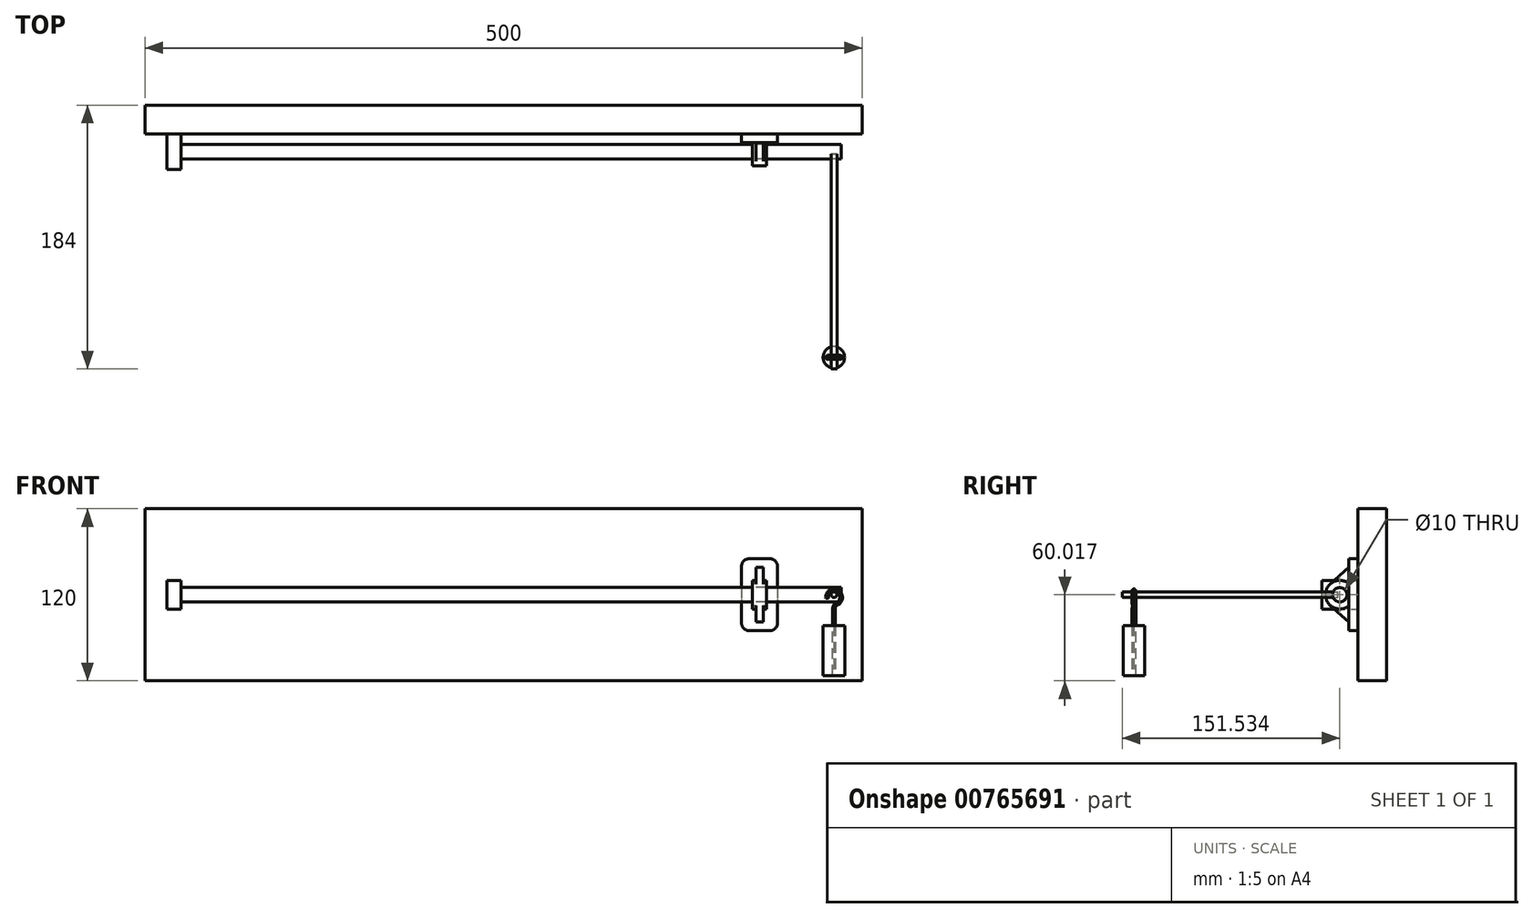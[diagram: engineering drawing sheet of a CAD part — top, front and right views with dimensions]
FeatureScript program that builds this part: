
annotation { "Feature Type Name" : "Feature", "Feature Type Description" : "" }
export const myFeature = defineFeature(function(context is Context, id is Id, definition is map)
    precondition{}
    {
        {
            var Q0;
            Q0=qCreatedBy(makeId("Front.planeOp"),FACE);
            var sketch = newSketch(context, id + "F0", { "sketchPlane" : qUnion([Q0])});
            skLineSegment(sketch, "E0.bottom", {"start": v(-32.37, 28.17) * mm, "end": v(467.63, 28.17) * mm});
            skLineSegment(sketch, "E0.top", {"start": v(-32.37, -91.83) * mm, "end": v(467.63, -91.83) * mm});
            skLineSegment(sketch, "E0.left", {"start": v(-32.37, 28.17) * mm, "end": v(-32.37, -91.83) * mm});
            skLineSegment(sketch, "E0.right", {"start": v(467.63, 28.17) * mm, "end": v(467.63, -91.83) * mm});
            skSolve(sketch);
        }
        {
            var Q0;
            Q0 = qSketchRegion(id + "F0", true);
            extrude(context, id + "F1", {"entities" : qUnion([Q0]), "endBound" : BoundingType.SYMMETRIC, "depth" : 20 * mm, "offsetDistance" : 25 * mm});
        }
        {
            var Q0;
            Q0=makeQuery(id+"F1.opExtrude","CAP_FACE",FACE,{"disambiguationData":[OSD([sQuery(id+"F0.wireOp",EDGE,"E0.bottom"),sQuery(id+"F0.wireOp",EDGE,"E0.top"),sQuery(id+"F0.wireOp",EDGE,"E0.left"),sQuery(id+"F0.wireOp",EDGE,"E0.right")])],"isStart":false});
            var sketch = newSketch(context, id + "F2", { "sketchPlane" : qUnion([Q0])});
            skLineSegment(sketch, "E1", {"start": v(-17.08, -31.83) * mm, "end": v(-17.08, -21.83) * mm});
            skLineSegment(sketch, "E2", {"start": v(-17.08, -21.83) * mm, "end": v(-17.08, -41.83) * mm});
            skLineSegment(sketch, "E3", {"start": v(-17.08, -41.83) * mm, "end": v(-7.08, -41.83) * mm});
            skLineSegment(sketch, "E4", {"start": v(-7.08, -41.83) * mm, "end": v(-7.08, -21.83) * mm});
            skLineSegment(sketch, "E5", {"start": v(-7.08, -21.83) * mm, "end": v(-17.08, -21.83) * mm});
            skPoint(sketch, "E6.start.orphan", {"position": v(-32.37, -31.83) * mm});
            skSolve(sketch);
        }
        {
            var Q0;
            Q0 = qSketchRegion(id + "F2", true);
            extrude(context, id + "F3", {"entities" : qUnion([Q0]), "operationType" : NewBodyOperationType.ADD, "depth" : 25 * mm, "offsetDistance" : 25 * mm});
        }
        {
            var Q0;
            Q0=makeQuery(id+"F3.opExtrude","SWEPT_FACE",FACE,{"disambiguationData":[OSD([sQuery(id+"F2.wireOp",EDGE,"E2")])]});
            var sketch = newSketch(context, id + "F4", { "sketchPlane" : qUnion([Q0])});
            skCircle(sketch, "E7", {"center": v(22.5, -31.83) * mm, "radius": 5 * mm});
            skPoint(sketch, "E7.centerSnap0", {"position": v(35, -31.83) * mm});
            skPoint(sketch, "E7.centerSnap1", {"position": v(22.5, -41.83) * mm});
            skSolve(sketch);
        }
        {
            var Q0;
            Q0=makeQuery(id+"F4.imprint","IMPRINT",FACE,{"disambiguationData":[TD([[makeQuery(id+"F4.imprint","IMPRINT",EDGE,{"derivedFrom":sQuery(id+"F4.wireOp",EDGE,"E7")}),1.0]])]});
            extrude(context, id + "F5", {"entities" : qUnion([Q0]), "operationType" : NewBodyOperationType.ADD, "oppositeDirection" : true, "depth" : 470 * mm, "offsetDistance" : 25 * mm});
        }
        {
            var Q0;
            Q0=qCreatedBy(makeId("Front.planeOp"),FACE);
            var sketch = newSketch(context, id + "F6", { "sketchPlane" : qUnion([Q0])});
            skCircle(sketch, "E8", {"center": v(-40.07, 52.74) * mm, "radius": 2 * mm});
            skSolve(sketch);
        }
        {
            var Q0;
            Q0 = qSketchRegion(id + "F6", true);
            extrude(context, id + "F7", {"entities" : qUnion([Q0]), "depth" : 150 * mm, "offsetDistance" : 25 * mm});
        }
        {
            var Q0;
            Q0=makeQuery(id+"F7.opExtrude","SWEPT_BODY",BODY,{"disambiguationData":[OSD([sQuery(id+"F6.wireOp",EDGE,"E8")])]});
            transform(context, id + "F8", {"entities" : qUnion([Q0]), "transformType" : TransformType.TRANSLATION_3D, "dx" : 488 * mm, "dy" : -24 * mm, "dz" : -84.5 * mm, "makeCopy" : false});
        }
        {
            var Q0;
            Q0=qCreatedBy(makeId("Right.planeOp"),FACE);
            var sketch = newSketch(context, id + "F9", { "sketchPlane" : qUnion([Q0])});
            skCircle(sketch, "E9", {"center": v(40.43, 44.24) * mm, "radius": 5 * mm});
            skArc(sketch, "E10", {"start": v(46.77, 51.97) * mm, "mid": v(30.43, 44.24) * mm, "end": v(46.77, 36.5) * mm});
            skLineSegment(sketch, "E11", {"start": v(52.93, 44.24) * mm, "end": v(52.93, 19.24) * mm});
            skLineSegment(sketch, "E12", {"start": v(52.93, 19.24) * mm, "end": v(52.93, 69.24) * mm});
            skLineSegment(sketch, "E13", {"start": v(52.93, 69.24) * mm, "end": v(46.77, 69.24) * mm});
            skLineSegment(sketch, "E14", {"start": v(46.77, 69.24) * mm, "end": v(46.77, 51.97) * mm});
            skLineSegment(sketch, "E15", {"start": v(46.77, 19.24) * mm, "end": v(52.93, 19.24) * mm});
            skLineSegment(sketch, "E16.trimOffspring", {"start": v(46.77, 36.5) * mm, "end": v(46.77, 19.24) * mm});
            skLineSegment(sketch, "E17", {"start": v(46.77, 69.24) * mm, "end": v(46.77, 63.24) * mm});
            skLineSegment(sketch, "E18", {"start": v(46.77, 63.24) * mm, "end": v(33.8, 51.72) * mm});
            skLineSegment(sketch, "E19", {"start": v(46.77, 19.24) * mm, "end": v(46.77, 25.24) * mm});
            skLineSegment(sketch, "E20", {"start": v(33.8, 36.76) * mm, "end": v(46.77, 25.24) * mm});
            skLineSegment(sketch, "E21", {"start": v(46.77, 51.97) * mm, "end": v(46.77, 36.5) * mm});
            skSolve(sketch);
        }
        {
            var Q0;
            Q0=makeQuery(id+"F9.imprint","IMPRINT",FACE,{"disambiguationData":[TD([[makeQuery(id+"F9.imprint","IMPRINT",EDGE,{"derivedFrom":sQuery(id+"F9.wireOp",EDGE,"E9")}),-1.0]])]});
            extrude(context, id + "F10", {"entities" : qUnion([Q0]), "endBound" : BoundingType.SYMMETRIC, "depth" : 10 * mm, "offsetDistance" : 25 * mm});
        }
        {
            var Q0;
            {var subQ0=sQuery(id+"F9.wireOp",EDGE,"E14");Q0=makeQuery(id+"F9.imprint","IMPRINT",FACE,{"disambiguationData":[TD([[makeQuery(id+"F9.imprint","IMPRINT",EDGE,{"derivedFrom":subQ0}),-1.0]])]});}
            var Q1;
            {var subQ0=sQuery(id+"F9.wireOp",EDGE,"E16.trimOffspring");Q1=makeQuery(id+"F9.imprint","IMPRINT",FACE,{"disambiguationData":[TD([[makeQuery(id+"F9.imprint","IMPRINT",EDGE,{"derivedFrom":subQ0}),-1.0]])]});}
            extrude(context, id + "F11", {"entities" : qUnion([Q0, Q1]), "operationType" : NewBodyOperationType.ADD, "endBound" : BoundingType.SYMMETRIC, "depth" : 5 * mm, "offsetDistance" : 25 * mm});
        }
        {
            var Q0;
            {var subQ1=sQuery(id+"F9.wireOp",EDGE,"E13");Q0=makeQuery(id+"F9.imprint","IMPRINT",FACE,{"disambiguationData":[TD([[makeQuery(id+"F9.imprint","IMPRINT",EDGE,{"derivedFrom":subQ1}),1.0]])]});}
            extrude(context, id + "F12", {"entities" : qUnion([Q0]), "operationType" : NewBodyOperationType.ADD, "endBound" : BoundingType.SYMMETRIC, "depth" : 25 * mm, "offsetDistance" : 25 * mm});
        }
        {
            var Q0;
            Q0=makeQuery(id+"F12.opExtrude","CAP_EDGE",EDGE,{"disambiguationData":[OSD([sQuery(id+"F9.wireOp",EDGE,"E13")])],"isStart":true});
            var Q1;
            Q1=makeQuery(id+"F12.opExtrude","CAP_EDGE",EDGE,{"disambiguationData":[OSD([sQuery(id+"F9.wireOp",EDGE,"E13")])],"isStart":false});
            var Q2;
            Q2=makeQuery(id+"F12.opExtrude","CAP_EDGE",EDGE,{"disambiguationData":[OSD([sQuery(id+"F9.wireOp",EDGE,"E15")])],"isStart":true});
            var Q3;
            Q3=makeQuery(id+"F12.opExtrude","CAP_EDGE",EDGE,{"disambiguationData":[OSD([sQuery(id+"F9.wireOp",EDGE,"E15")])],"isStart":false});
            fillet(context, id + "F13", {"entities" : qUnion([Q0, Q1, Q2, Q3]), "radius" : 5 * mm, "tangentPropagation" : true, "allowEdgeOverflow" : false});
        }
        {
            var Q0;
            Q0=makeQuery(id+"F10.opExtrude","SWEPT_BODY",BODY,{"disambiguationData":[OSD([sQuery(id+"F9.wireOp",EDGE,"E9"),sQuery(id+"F9.wireOp",EDGE,"E10"),sQuery(id+"F9.wireOp",EDGE,"E21")])]});
            transform(context, id + "F14", {"entities" : qUnion([Q0]), "transformType" : TransformType.TRANSLATION_3D, "dx" : 396 * mm, "dy" : -62.9 * mm, "dz" : -76.05 * mm, "makeCopy" : false});
        }
        {
            var Q0;
            Q0=qCreatedBy(makeId("Front.planeOp"),FACE);
            var sketch = newSketch(context, id + "F15", { "sketchPlane" : qUnion([Q0])});
            skArc(sketch, "E22", {"start": v(-52.14, 43.02) * mm, "mid": v(-52.02, 50.13) * mm, "end": v(-57.9, 46.13) * mm});
            skArc(sketch, "E23", {"start": v(-51.67, 41.05) * mm, "mid": v(-50.87, 51.77) * mm, "end": v(-59.88, 45.9) * mm});
            skLineSegment(sketch, "E24", {"start": v(-54.92, 13.23) * mm, "end": v(-54.92, 38.55) * mm});
            skLineSegment(sketch, "E25", {"start": v(-52.92, 13.23) * mm, "end": v(-52.92, 39.2) * mm});
            skLineSegment(sketch, "E26", {"start": v(-57.9, 46.13) * mm, "end": v(-59.88, 45.9) * mm});
            skPoint(sketch, "E27.visualSharp", {"position": v(-54.92, 42.73) * mm});
            skArc(sketch, "E27.filletArc", {"start": v(-52.14, 43.02) * mm, "mid": v(-54.17, 41.18) * mm, "end": v(-54.92, 38.55) * mm});
            skPoint(sketch, "E28.visualSharp", {"position": v(-52.92, 40.7) * mm});
            skArc(sketch, "E28.filletArc", {"start": v(-51.67, 41.05) * mm, "mid": v(-52.58, 40.3) * mm, "end": v(-52.92, 39.2) * mm});
            skLineSegment(sketch, "E29", {"start": v(-52.92, 13.23) * mm, "end": v(-52.92, -7.83) * mm});
            skLineSegment(sketch, "E30", {"start": v(-52.92, -7.83) * mm, "end": v(-54.92, -7.83) * mm});
            skLineSegment(sketch, "E31", {"start": v(-54.92, -7.83) * mm, "end": v(-54.92, 13.23) * mm});
            skSolve(sketch);
        }
        {
            var Q0;
            Q0=makeQuery(id+"F15.imprint","IMPRINT",FACE,{"disambiguationData":[TD([[makeQuery(id+"F15.imprint","IMPRINT",EDGE,{"derivedFrom":sQuery(id+"F15.wireOp",EDGE,"E22")}),-1.0]])]});
            extrude(context, id + "F16", {"entities" : qUnion([Q0]), "endBound" : BoundingType.SYMMETRIC, "depth" : 3 * mm, "offsetDistance" : 25 * mm});
        }
        {
            var Q0;
            Q0=makeQuery(id+"F16.opExtrude","CAP_EDGE",EDGE,{"disambiguationData":[OSD([sQuery(id+"F15.wireOp",EDGE,"E23")])],"isStart":false});
            var Q1;
            Q1=makeQuery(id+"F16.opExtrude","CAP_EDGE",EDGE,{"disambiguationData":[OSD([sQuery(id+"F15.wireOp",EDGE,"E23")])],"isStart":true});
            var Q2;
            Q2=makeQuery(id+"F16.opExtrude","CAP_EDGE",EDGE,{"disambiguationData":[OSD([sQuery(id+"F15.wireOp",EDGE,"E22")])],"isStart":false});
            var Q3;
            Q3=makeQuery(id+"F16.opExtrude","CAP_EDGE",EDGE,{"disambiguationData":[OSD([sQuery(id+"F15.wireOp",EDGE,"E27.filletArc")])],"isStart":false});
            var Q4;
            Q4=makeQuery(id+"F16.opExtrude","CAP_EDGE",EDGE,{"disambiguationData":[OSD([sQuery(id+"F15.wireOp",EDGE,"E25")])],"isStart":false});
            fillet(context, id + "F17", {"entities" : qUnion([Q0, Q1, Q2, Q3, Q4]), "radius" : 2 * mm, "tangentPropagation" : true, "allowEdgeOverflow" : false});
        }
        {
            var Q0;
            Q0=makeQuery(id+"F16.opExtrude","SWEPT_BODY",BODY,{"disambiguationData":[OSD([sQuery(id+"F15.wireOp",EDGE,"E22"),sQuery(id+"F15.wireOp",EDGE,"E23"),sQuery(id+"F15.wireOp",EDGE,"E24"),sQuery(id+"F15.wireOp",EDGE,"E25"),sQuery(id+"F15.wireOp",EDGE,"E26"),sQuery(id+"F15.wireOp",EDGE,"E27.filletArc"),sQuery(id+"F15.wireOp",EDGE,"E28.filletArc"),sQuery(id+"F15.wireOp",EDGE,"E29"),sQuery(id+"F15.wireOp",EDGE,"E30"),sQuery(id+"F15.wireOp",EDGE,"E31")])]});
            transform(context, id + "F18", {"entities" : qUnion([Q0]), "transformType" : TransformType.TRANSLATION_3D, "dx" : 501.8 * mm, "dy" : -166 * mm, "dz" : -80.3 * mm, "makeCopy" : false});
        }
        {
            var Q0;
            Q0=qCreatedBy(makeId("Top.planeOp"),FACE);
            var sketch = newSketch(context, id + "F19", { "sketchPlane" : qUnion([Q0])});
            skCircle(sketch, "E32", {"center": v(29.7, 36.96) * mm, "radius": 7.5 * mm});
            skSolve(sketch);
        }
        {
            var Q0;
            Q0=makeQuery(id+"F19.imprint","IMPRINT",FACE,{"disambiguationData":[TD([[makeQuery(id+"F19.imprint","IMPRINT",EDGE,{"derivedFrom":sQuery(id+"F19.wireOp",EDGE,"E32")}),1.0]])]});
            extrude(context, id + "F20", {"entities" : qUnion([Q0]), "endBound" : BoundingType.SYMMETRIC, "depth" : 35 * mm, "offsetDistance" : 25 * mm});
        }
        {
            var Q0;
            Q0=makeQuery(id+"F20.opExtrude","SWEPT_BODY",BODY,{"disambiguationData":[OSD([sQuery(id+"F19.wireOp",EDGE,"E32")])]});
            transform(context, id + "F21", {"entities" : qUnion([Q0]), "transformType" : TransformType.TRANSLATION_3D, "dx" : 418.1 * mm, "dy" : -202.9 * mm, "dz" : -70.8 * mm, "makeCopy" : false});
        }
        {
            var Q0;
            Q0=makeQuery(id+"F1.opExtrude","SWEPT_BODY",BODY,{"disambiguationData":[OSD([sQuery(id+"F0.wireOp",EDGE,"E0.bottom"),sQuery(id+"F0.wireOp",EDGE,"E0.top"),sQuery(id+"F0.wireOp",EDGE,"E0.left"),sQuery(id+"F0.wireOp",EDGE,"E0.right")])]});
            var Q1;
            Q1=makeQuery(id+"F7.opExtrude","SWEPT_BODY",BODY,{"disambiguationData":[OSD([sQuery(id+"F6.wireOp",EDGE,"E8")])]});
            var Q2;
            Q2=makeQuery(id+"F10.opExtrude","SWEPT_BODY",BODY,{"disambiguationData":[OSD([sQuery(id+"F9.wireOp",EDGE,"E9"),sQuery(id+"F9.wireOp",EDGE,"E10"),sQuery(id+"F9.wireOp",EDGE,"E21")])]});
            var Q3;
            Q3=makeQuery(id+"F16.opExtrude","SWEPT_BODY",BODY,{"disambiguationData":[OSD([sQuery(id+"F15.wireOp",EDGE,"E22"),sQuery(id+"F15.wireOp",EDGE,"E23"),sQuery(id+"F15.wireOp",EDGE,"E24"),sQuery(id+"F15.wireOp",EDGE,"E25"),sQuery(id+"F15.wireOp",EDGE,"E26"),sQuery(id+"F15.wireOp",EDGE,"E27.filletArc"),sQuery(id+"F15.wireOp",EDGE,"E28.filletArc"),sQuery(id+"F15.wireOp",EDGE,"E29"),sQuery(id+"F15.wireOp",EDGE,"E30"),sQuery(id+"F15.wireOp",EDGE,"E31")])]});
            var Q4;
            Q4=makeQuery(id+"F20.opExtrude","SWEPT_BODY",BODY,{"disambiguationData":[OSD([sQuery(id+"F19.wireOp",EDGE,"E32")])]});
            transform(context, id + "F22", {"entities" : qUnion([Q0, Q1, Q2, Q3, Q4]), "transformType" : TransformType.TRANSLATION_3D, "dx" : 411 * mm, "dy" : 0 * mm, "dz" : 0 * mm, "makeCopy" : false});
        }
    });
